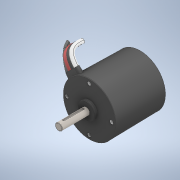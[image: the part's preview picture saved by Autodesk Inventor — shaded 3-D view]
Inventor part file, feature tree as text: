
AUTODESK INVENTOR PART (.ipt)
format: ipt  version: 2020 (Build 240168000, 168)  size: 459,264 bytes
history: native  units: in
note: dims shown in document units (in); Inventor stores cm internally (conversion verified against a paired STEP export)
features: boolean_combine x1, revolve x1, sketch x1
ambient origin geometry x8: Origin, YZ Plane, XZ Plane, XY Plane, X Axis, Y Axis, Z Axis, Center Point
bodies: Solid1 (feature_tree)
feature tree (3):
  boolean_combine  "Combine1"
  revolve  "Revolution1"  [1 undecoded]
  sketch  "Sketch2"  dims[d0=90.0deg]
note: 1 required parameter value undecoded (feature->parameter linkage not recoverable at this tier; creation-order binding heuristic only, values carry confidence <= 0.55)
